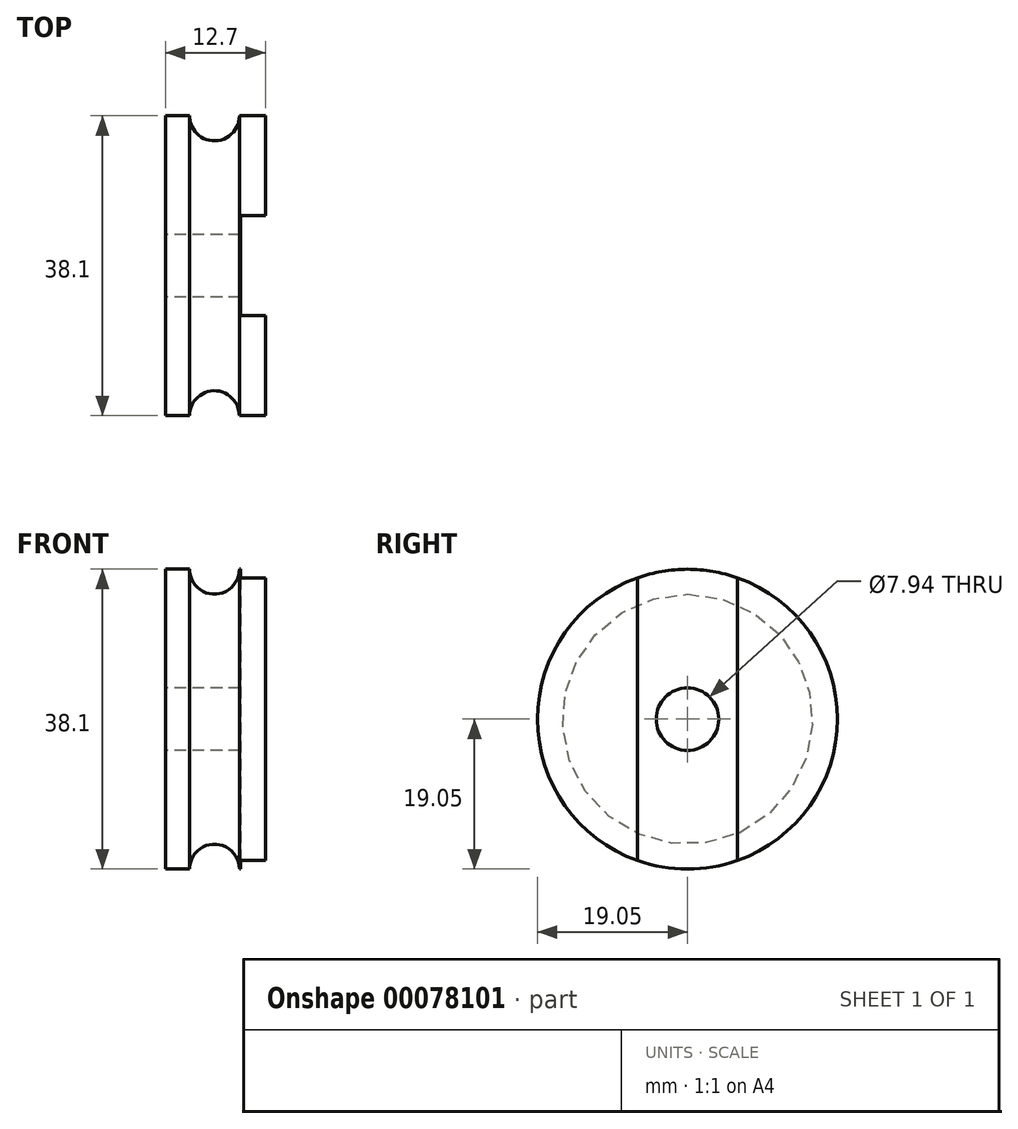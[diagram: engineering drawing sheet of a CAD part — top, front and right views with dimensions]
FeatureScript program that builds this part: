
annotation { "Feature Type Name" : "Feature", "Feature Type Description" : "" }
export const myFeature = defineFeature(function(context is Context, id is Id, definition is map)
    precondition{}
    {
        {
            var Q0;
            Q0=qCreatedBy(makeId("Front.planeOp"),FACE);
            var sketch = newSketch(context, id + "F0", { "sketchPlane" : qUnion([Q0])});
            skLineSegment(sketch, "E0", {"start": v(-6.22, 0) * mm, "end": v(-6.22, 19.05) * mm});
            skLineSegment(sketch, "E1", {"start": v(6.48, 0) * mm, "end": v(6.48, 19.05) * mm});
            skLineSegment(sketch, "E2", {"start": v(-6.22, 0) * mm, "end": v(6.48, 0) * mm});
            skArc(sketch, "E3", {"start": v(3.18, 19.05) * mm, "mid": v(0, 15.87) * mm, "end": v(-3.18, 19.05) * mm});
            skLineSegment(sketch, "E4", {"start": v(-6.22, 19.05) * mm, "end": v(-3.18, 19.05) * mm});
            skLineSegment(sketch, "E5", {"start": v(3.17, 19.05) * mm, "end": v(6.48, 19.05) * mm});
            skSolve(sketch);
        }
        {
            var Q0;
            Q0=makeQuery(id+"F0.imprint","IMPRINT",FACE,{"disambiguationData":[TD([[makeQuery(id+"F0.imprint","IMPRINT",EDGE,{"derivedFrom":sQuery(id+"F0.wireOp",EDGE,"E0")}),-1.0]])]});
            var Q1;
            Q1=sQuery(id+"F0.wireOp",EDGE,"E2");
            revolve(context, id + "F1", {"entities" : qUnion([Q0]), "axis" : qUnion([Q1]), "revolveType" : RevolveType.FULL});
        }
        {
            var Q0;
            Q0=makeQuery(id+"F1.opRevolve","SWEPT_FACE",FACE,{"disambiguationData":[OSD([sQuery(id+"F0.wireOp",EDGE,"E1")])]});
            var sketch = newSketch(context, id + "F2", { "sketchPlane" : qUnion([Q0])});
            skLineSegment(sketch, "E6.bottom", {"start": v(-6.35, 25.4) * mm, "end": v(6.35, 25.4) * mm});
            skLineSegment(sketch, "E6.top", {"start": v(-6.35, -25.4) * mm, "end": v(6.35, -25.4) * mm});
            skLineSegment(sketch, "E6.left", {"start": v(-6.35, 25.4) * mm, "end": v(-6.35, -25.4) * mm});
            skLineSegment(sketch, "E6.right", {"start": v(6.35, 25.4) * mm, "end": v(6.35, -25.4) * mm});
            skPoint(sketch, "E6.middle", {"position": v(0, 0) * mm});
            skCircle(sketch, "E7", {"center": v(0, 0) * mm, "radius": 3.97 * mm});
            skSolve(sketch);
        }
        {
            var Q0;
            Q0=makeQuery(id+"F2.imprint","IMPRINT",FACE,{"disambiguationData":[TD([[makeQuery(id+"F2.imprint","IMPRINT",EDGE,{"derivedFrom":sQuery(id+"F2.wireOp",EDGE,"E7")}),-1.0]])]});
            extrude(context, id + "F3", {"entities" : qUnion([Q0]), "operationType" : NewBodyOperationType.REMOVE, "oppositeDirection" : true, "depth" : 3.17 * mm});
        }
        {
            var Q0;
            Q0=makeQuery(id+"F1.opRevolve","SWEPT_FACE",FACE,{"disambiguationData":[OSD([sQuery(id+"F0.wireOp",EDGE,"E0")])]});
            var sketch = newSketch(context, id + "F4", { "sketchPlane" : qUnion([Q0])});
            skCircle(sketch, "E8", {"center": v(0, 0) * mm, "radius": 3.97 * mm});
            skSolve(sketch);
        }
        {
            var Q0;
            Q0=makeQuery(id+"F4.imprint","IMPRINT",FACE,{"disambiguationData":[TD([[makeQuery(id+"F4.imprint","IMPRINT",EDGE,{"derivedFrom":sQuery(id+"F4.wireOp",EDGE,"E8")}),1.0]])]});
            extrude(context, id + "F5", {"entities" : qUnion([Q0]), "operationType" : NewBodyOperationType.REMOVE, "endBound" : BoundingType.THROUGH_ALL, "oppositeDirection" : true, "depth" : 25.4 * mm});
        }
    });
